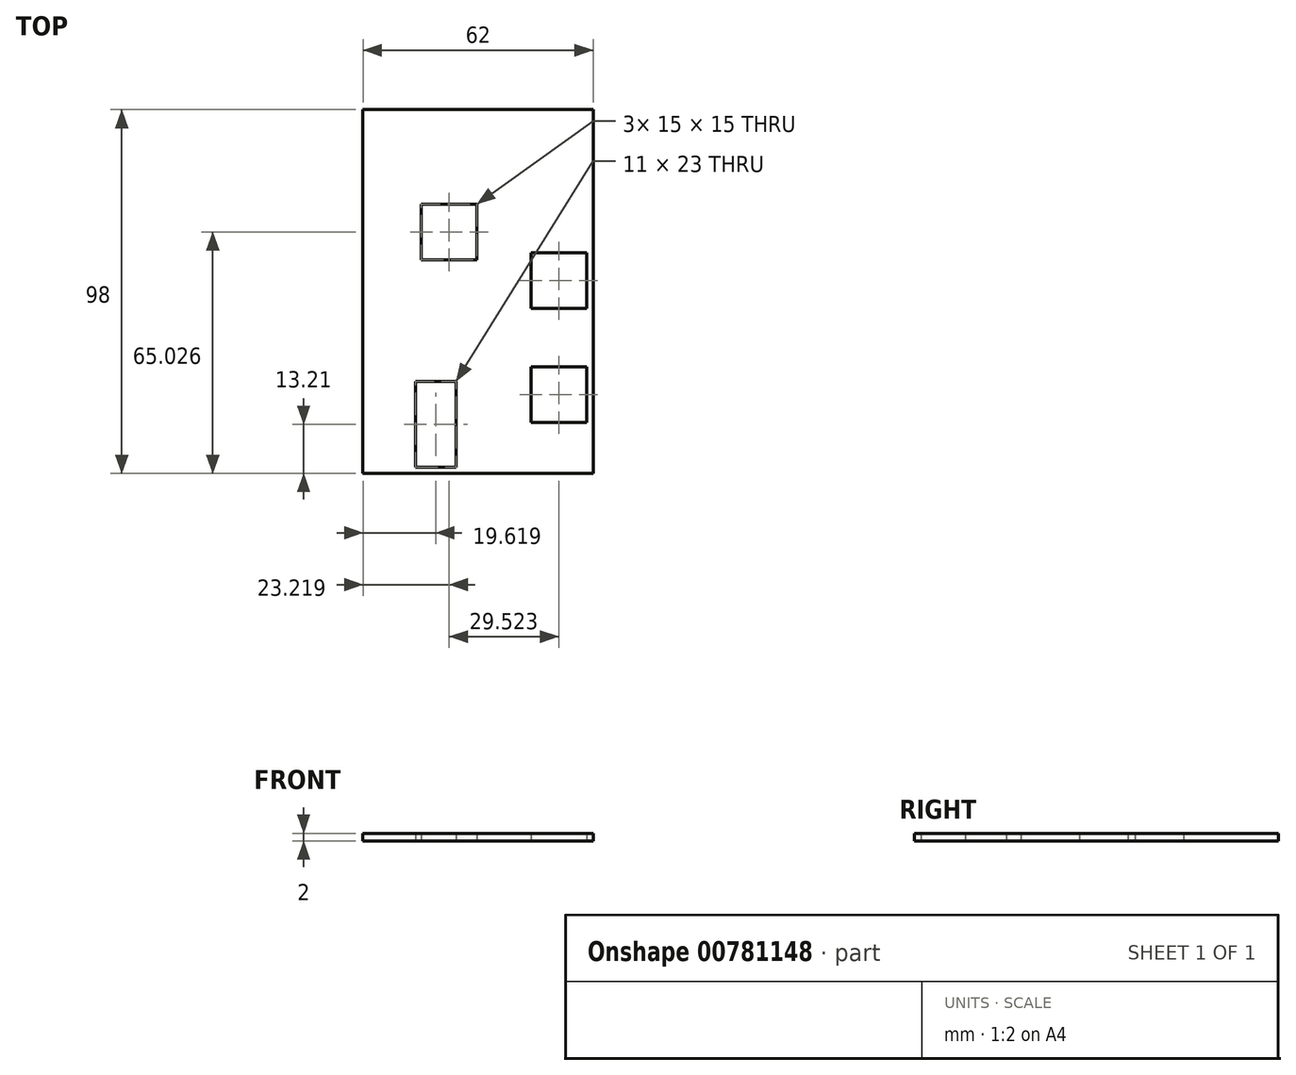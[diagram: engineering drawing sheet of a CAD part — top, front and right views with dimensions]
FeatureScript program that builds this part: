
annotation { "Feature Type Name" : "Feature", "Feature Type Description" : "" }
export const myFeature = defineFeature(function(context is Context, id is Id, definition is map)
    precondition{}
    {
        {
            var Q0;
            Q0=qCreatedBy(makeId("Top.planeOp"),FACE);
            var sketch = newSketch(context, id + "F0", { "sketchPlane" : qUnion([Q0])});
            skLineSegment(sketch, "E0.bottom", {"start": v(-41.75, 73.29) * mm, "end": v(20.25, 73.29) * mm});
            skLineSegment(sketch, "E0.top", {"start": v(-41.75, -24.71) * mm, "end": v(20.25, -24.71) * mm});
            skLineSegment(sketch, "E0.left", {"start": v(-41.75, 73.29) * mm, "end": v(-41.75, -24.71) * mm});
            skLineSegment(sketch, "E0.right", {"start": v(20.25, 73.29) * mm, "end": v(20.25, -24.71) * mm});
            skSolve(sketch);
        }
        {
            var Q0;
            Q0=makeQuery(id+"F0.imprint","IMPRINT",FACE,{"disambiguationData":[TD([[makeQuery(id+"F0.imprint","IMPRINT",EDGE,{"derivedFrom":sQuery(id+"F0.wireOp",EDGE,"E0.bottom")}),-1.0]])]});
            var sketch = newSketch(context, id + "F1", { "sketchPlane" : qUnion([Q0])});
            skLineSegment(sketch, "E1.bottom", {"start": v(-27.63, -23) * mm, "end": v(-16.63, -23) * mm});
            skLineSegment(sketch, "E1.top", {"start": v(-27.63, 0) * mm, "end": v(-16.63, 0) * mm});
            skLineSegment(sketch, "E1.left", {"start": v(-27.63, -23) * mm, "end": v(-27.63, 0) * mm});
            skLineSegment(sketch, "E1.right", {"start": v(-16.63, -23) * mm, "end": v(-16.63, 0) * mm});
            skLineSegment(sketch, "E2.bottom", {"start": v(3.5, -11.04) * mm, "end": v(18.5, -11.04) * mm});
            skLineSegment(sketch, "E2.top", {"start": v(3.5, 3.96) * mm, "end": v(18.5, 3.96) * mm});
            skLineSegment(sketch, "E2.left", {"start": v(3.5, -11.04) * mm, "end": v(3.5, 3.96) * mm});
            skLineSegment(sketch, "E2.right", {"start": v(18.5, -11.04) * mm, "end": v(18.5, 3.96) * mm});
            skLineSegment(sketch, "E3.bottom", {"start": v(3.5, 34.7) * mm, "end": v(18.5, 34.7) * mm});
            skLineSegment(sketch, "E3.top", {"start": v(3.5, 19.7) * mm, "end": v(18.5, 19.7) * mm});
            skLineSegment(sketch, "E3.left", {"start": v(3.5, 34.7) * mm, "end": v(3.5, 19.7) * mm});
            skLineSegment(sketch, "E3.right", {"start": v(18.5, 34.7) * mm, "end": v(18.5, 19.7) * mm});
            skLineSegment(sketch, "E4.bottom", {"start": v(-26.03, 47.82) * mm, "end": v(-11.03, 47.82) * mm});
            skLineSegment(sketch, "E4.top", {"start": v(-26.03, 32.82) * mm, "end": v(-11.03, 32.82) * mm});
            skLineSegment(sketch, "E4.left", {"start": v(-26.03, 47.82) * mm, "end": v(-26.03, 32.82) * mm});
            skLineSegment(sketch, "E4.right", {"start": v(-11.03, 47.82) * mm, "end": v(-11.03, 32.82) * mm});
            skSolve(sketch);
        }
        {
            var Q0;
            Q0=makeQuery(id+"F1.imprint","IMPRINT",FACE,{"disambiguationData":[TD([[makeQuery(id+"F1.imprint","IMPRINT",EDGE,{"derivedFrom":sQuery(id+"F1.wireOp",EDGE,"E1.bottom")}),-1.0]])]});
            extrude(context, id + "F2", {"entities" : qUnion([Q0]), "depth" : 2 * mm, "offsetDistance" : 25 * mm});
        }
    });
